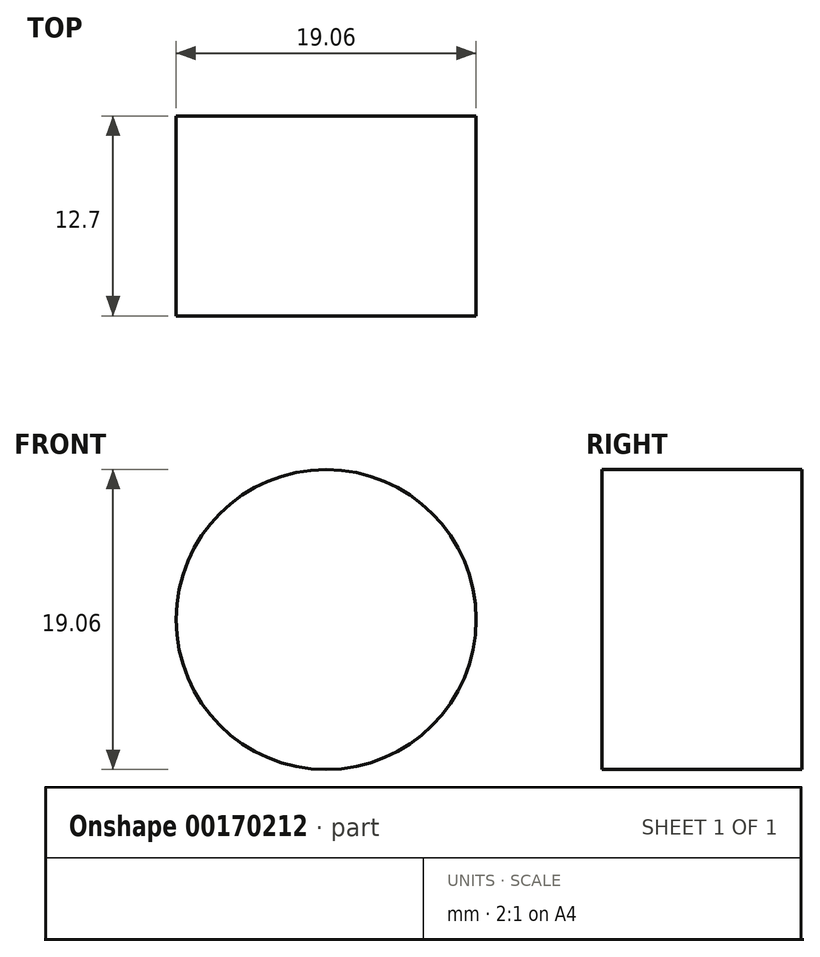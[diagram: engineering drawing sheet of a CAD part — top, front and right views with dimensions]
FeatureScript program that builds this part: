
annotation { "Feature Type Name" : "Feature", "Feature Type Description" : "" }
export const myFeature = defineFeature(function(context is Context, id is Id, definition is map)
    precondition{}
    {
        {
            var Q0;
            Q0=qCreatedBy(makeId("Front.planeOp"),FACE);
            var sketch = newSketch(context, id + "F0", { "sketchPlane" : qUnion([Q0])});
            skCircle(sketch, "E0", {"center": v(0, 0) * mm, "radius": 9.53 * mm});
            skSolve(sketch);
        }
        {
            var Q0;
            Q0 = qSketchRegion(id + "F0", true);
            extrude(context, id + "F1", {"entities" : qUnion([Q0]), "oppositeDirection" : true, "depth" : 12.7 * mm});
        }
    });
